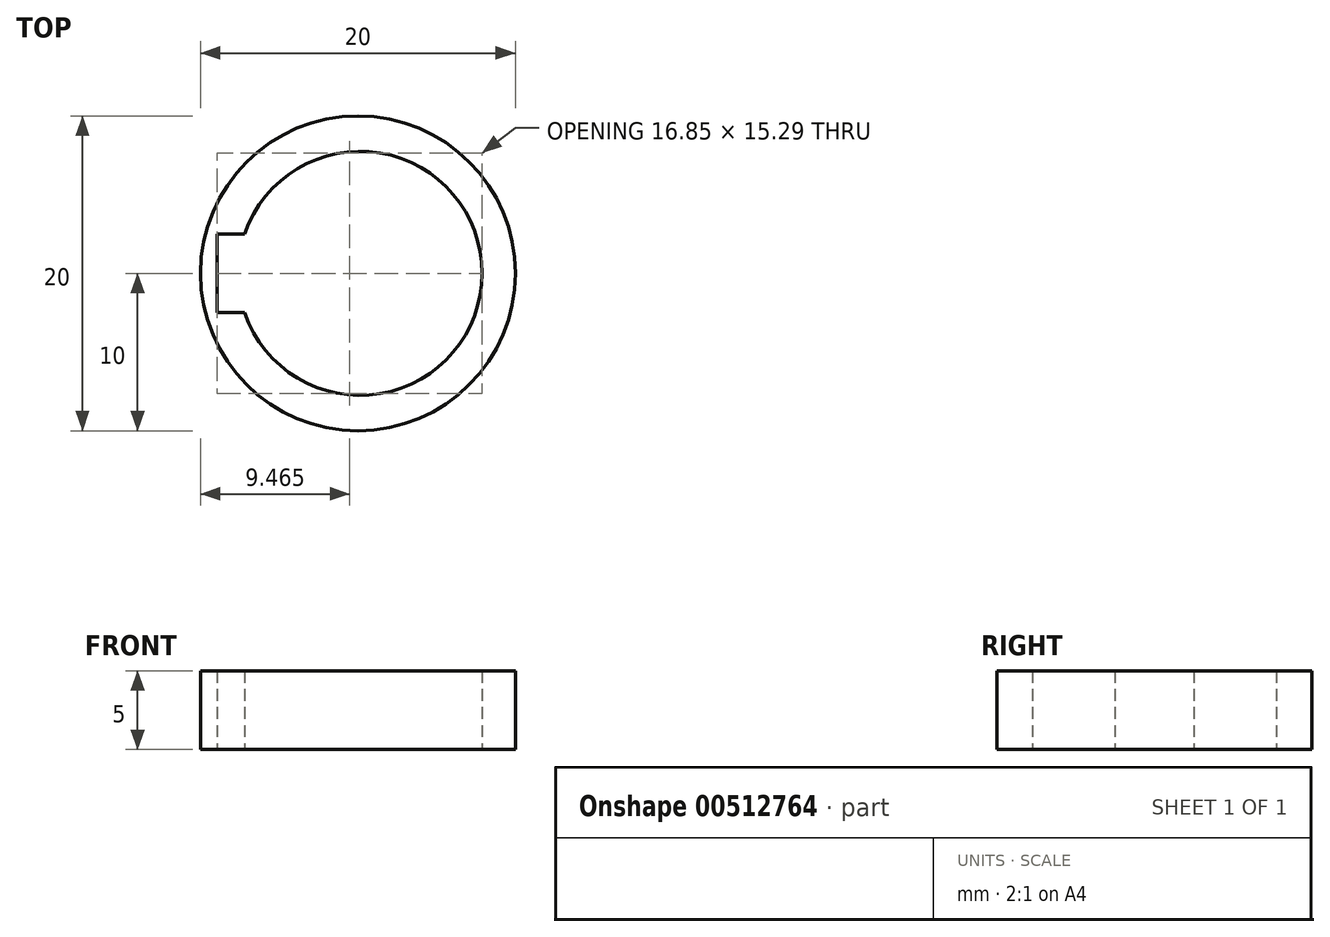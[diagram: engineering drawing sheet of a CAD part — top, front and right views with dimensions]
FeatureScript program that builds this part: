
annotation { "Feature Type Name" : "Feature", "Feature Type Description" : "" }
export const myFeature = defineFeature(function(context is Context, id is Id, definition is map)
    precondition{}
    {
        {
            var Q0;
            Q0=qCreatedBy(makeId("Top.planeOp"),FACE);
            var sketch = newSketch(context, id + "F0", { "sketchPlane" : qUnion([Q0])});
            skCircle(sketch, "E0", {"center": v(0.14, 0) * mm, "radius": 7.75 * mm});
            skSolve(sketch);
        }
        {
            var Q0;
            Q0=qCreatedBy(makeId("Top.planeOp"),FACE);
            var sketch = newSketch(context, id + "F1", { "sketchPlane" : qUnion([Q0])});
            skCircle(sketch, "E1", {"center": v(0, 0) * mm, "radius": 10 * mm});
            skSolve(sketch);
        }
        {
            var Q0;
            Q0=makeQuery(id+"F1.imprint","IMPRINT",FACE,{"disambiguationData":[TD([[makeQuery(id+"F1.imprint","IMPRINT",EDGE,{"derivedFrom":sQuery(id+"F1.wireOp",EDGE,"E1")}),1.0]])]});
            extrude(context, id + "F2", {"entities" : qUnion([Q0]), "depth" : 5 * mm});
        }
        {
            var Q0;
            Q0 = qSketchRegion(id + "F0", true);
            extrude(context, id + "F3", {"entities" : qUnion([Q0]), "operationType" : NewBodyOperationType.REMOVE, "depth" : 25.4 * mm});
        }
        {
            var Q0;
            Q0=qCreatedBy(makeId("Top.planeOp"),FACE);
            var sketch = newSketch(context, id + "F4", { "sketchPlane" : qUnion([Q0])});
            skLineSegment(sketch, "E2", {"start": v(0, -2.5) * mm, "end": v(-8.96, -2.5) * mm});
            skLineSegment(sketch, "E3", {"start": v(-8.96, -2.5) * mm, "end": v(-8.96, 2.5) * mm});
            skLineSegment(sketch, "E4", {"start": v(-8.96, 2.5) * mm, "end": v(0, 2.5) * mm});
            skLineSegment(sketch, "E5", {"start": v(0, -2.5) * mm, "end": v(0, 2.5) * mm});
            skSolve(sketch);
        }
        {
            var Q0;
            Q0 = qSketchRegion(id + "F4", true);
            extrude(context, id + "F5", {"entities" : qUnion([Q0]), "operationType" : NewBodyOperationType.REMOVE, "depth" : 80 * mm});
        }
    });
